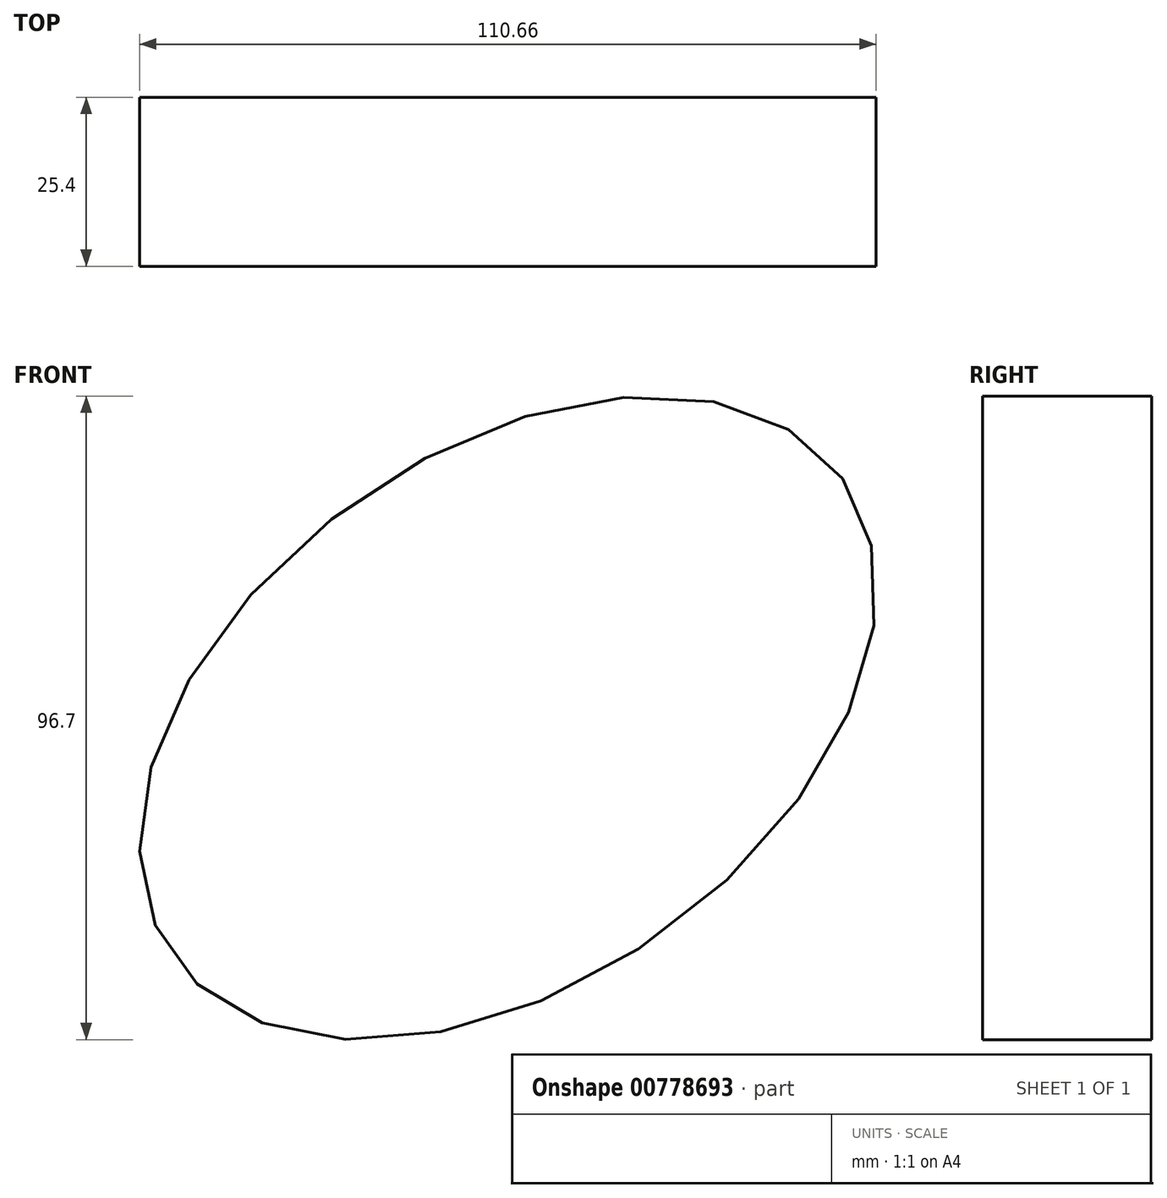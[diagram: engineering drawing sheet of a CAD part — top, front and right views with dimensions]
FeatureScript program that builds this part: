
annotation { "Feature Type Name" : "Feature", "Feature Type Description" : "" }
export const myFeature = defineFeature(function(context is Context, id is Id, definition is map)
    precondition{}
    {
        {
            var Q0;
            Q0=qCreatedBy(makeId("Front.planeOp"),FACE);
            var sketch = newSketch(context, id + "F0", { "sketchPlane" : qUnion([Q0])});
            skEllipse(sketch, "E0", {"center": v(0, 0) * mm, "majorRadius": 61.78 * mm, "minorRadius": 39.78 * mm, "majorAxis": v(0.81, 0.58)});
            skSolve(sketch);
        }
        {
            var Q0;
            Q0=sQuery(id+"F0.wireOp",EDGE,"E0");
            extrude(context, id + "F1", {"bodyType" : ToolBodyType.SURFACE, "surfaceEntities" : qUnion([Q0]), "depth" : 25.4 * mm, "offsetDistance" : 25.4 * mm});
        }
    });
